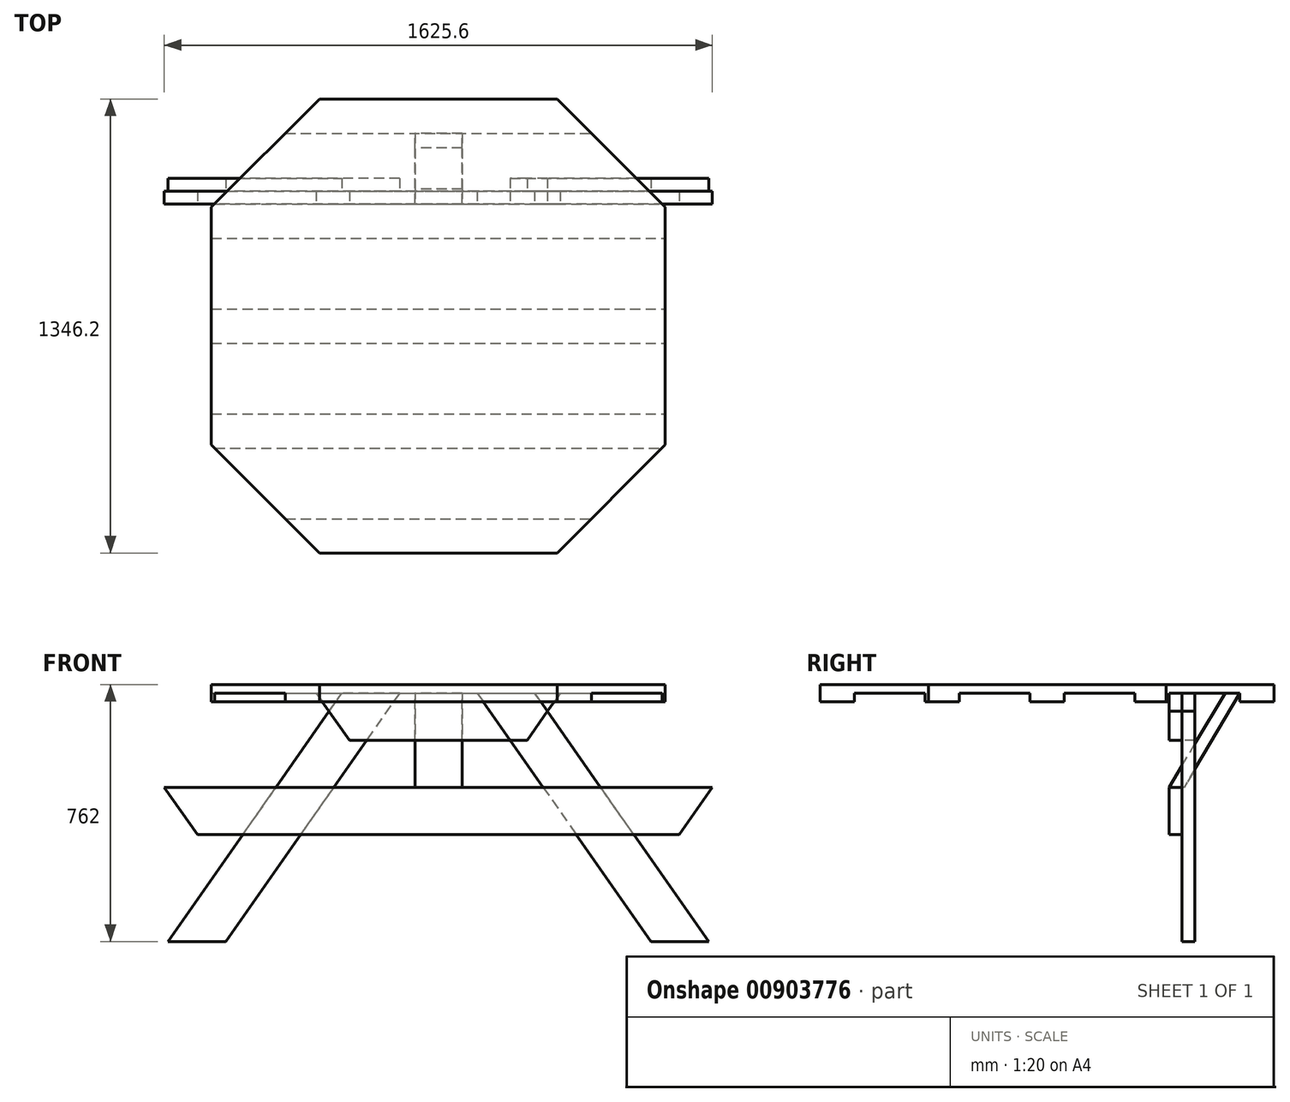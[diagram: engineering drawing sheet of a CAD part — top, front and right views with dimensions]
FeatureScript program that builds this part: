
annotation { "Feature Type Name" : "Feature", "Feature Type Description" : "" }
export const myFeature = defineFeature(function(context is Context, id is Id, definition is map)
    precondition{}
    {
        {
            var Q0;
            Q0=qCreatedBy(makeId("Top.planeOp"),FACE);
            var sketch = newSketch(context, id + "F0", { "sketchPlane" : qUnion([Q0])});
            skPoint(sketch, "E0.middle", {"position": v(0, 0) * mm});
            skLineSegment(sketch, "E1", {"start": v(-362.6, 663.57) * mm, "end": v(-362.6, -663.58) * mm});
            skLineSegment(sketch, "E2", {"start": v(361.3, 663.58) * mm, "end": v(361.3, -663.58) * mm});
            skLineSegment(sketch, "E3", {"start": v(-0.66, 673.1) * mm, "end": v(-0.66, -673.1) * mm});
            skPoint(sketch, "E4", {"position": v(-673.76, 0) * mm});
            skPoint(sketch, "E5", {"position": v(672.44, 0) * mm});
            skLineSegment(sketch, "E6", {"start": v(-673.76, 352.43) * mm, "end": v(-673.76, -352.43) * mm});
            skLineSegment(sketch, "E7", {"start": v(672.44, 352.43) * mm, "end": v(672.44, -352.43) * mm});
            skLineSegment(sketch, "E8", {"start": v(-353.08, -673.1) * mm, "end": v(351.77, -673.1) * mm});
            skLineSegment(sketch, "E9", {"start": v(-353.08, 673.1) * mm, "end": v(351.77, 673.1) * mm});
            skPoint(sketch, "E10", {"position": v(-0.66, -673.1) * mm});
            skPoint(sketch, "E11", {"position": v(-0.66, 673.1) * mm});
            skLineSegment(sketch, "E12", {"start": v(-673.76, 352.43) * mm, "end": v(-353.08, 673.1) * mm});
            skLineSegment(sketch, "E13", {"start": v(351.77, 673.1) * mm, "end": v(672.44, 352.42) * mm});
            skLineSegment(sketch, "E14", {"start": v(351.77, -673.1) * mm, "end": v(672.44, -352.43) * mm});
            skLineSegment(sketch, "E15", {"start": v(-353.08, -673.1) * mm, "end": v(-673.76, -352.43) * mm});
            skLineSegment(sketch, "E16", {"start": v(-454.68, -571.5) * mm, "end": v(453.37, -571.5) * mm});
            skLineSegment(sketch, "E17", {"start": v(-673.76, 50.8) * mm, "end": v(672.44, 50.8) * mm});
            skLineSegment(sketch, "E18", {"start": v(-673.76, -50.8) * mm, "end": v(672.44, -50.8) * mm});
            skLineSegment(sketch, "E19", {"start": v(-673.76, 260.35) * mm, "end": v(672.44, 260.35) * mm});
            skLineSegment(sketch, "E20", {"start": v(-673.76, -260.35) * mm, "end": v(672.44, -260.35) * mm});
            skLineSegment(sketch, "E21", {"start": v(-454.68, 571.5) * mm, "end": v(453.37, 571.5) * mm});
            skLineSegment(sketch, "E22", {"start": v(-664.23, -361.95) * mm, "end": v(662.92, -361.95) * mm});
            skLineSegment(sketch, "E23", {"start": v(-664.23, 361.95) * mm, "end": v(662.92, 361.95) * mm});
            skSolve(sketch);
        }
        {
            var Q0;
            {var subQ0=sQuery(id+"F0.wireOp",EDGE,"E12");var subQ1=sQuery(id+"F0.wireOp",EDGE,"E1");var subQ2=makeQuery(id+"F0.imprint","INTERSECT",VERTEX,{"derivedFrom":[subQ1,subQ0]});Q0=makeQuery(id+"F0.imprint","IMPRINT",FACE,{"disambiguationData":[TD([[makeQuery(id+"F0.imprint","IMPRINT",EDGE,{"disambiguationData":[TD([[subQ2,-1.0]])],"derivedFrom":subQ1}),-1.0]])]});}
            var Q1;
            {var subQ3=sQuery(id+"F0.wireOp",EDGE,"E1");var subQ7=sQuery(id+"F0.wireOp",EDGE,"E23");var subQ9=makeQuery(id+"F0.imprint","INTERSECT",VERTEX,{"derivedFrom":[subQ3,subQ7]});Q1=makeQuery(id+"F0.imprint","IMPRINT",FACE,{"disambiguationData":[TD([[makeQuery(id+"F0.imprint","IMPRINT",EDGE,{"disambiguationData":[TD([[subQ9,-1.0]])],"derivedFrom":subQ3}),-1.0]])]});}
            var Q2;
            {var subQ0=sQuery(id+"F0.wireOp",EDGE,"E17");var subQ1=sQuery(id+"F0.wireOp",EDGE,"E1");var subQ2=makeQuery(id+"F0.imprint","INTERSECT",VERTEX,{"derivedFrom":[subQ1,subQ0]});Q2=makeQuery(id+"F0.imprint","IMPRINT",FACE,{"disambiguationData":[TD([[makeQuery(id+"F0.imprint","IMPRINT",EDGE,{"disambiguationData":[TD([[subQ2,-1.0]])],"derivedFrom":subQ1}),-1.0]])]});}
            var Q3;
            {var subQ0=sQuery(id+"F0.wireOp",EDGE,"E20");var subQ3=sQuery(id+"F0.wireOp",EDGE,"E1");var subQ4=makeQuery(id+"F0.imprint","INTERSECT",VERTEX,{"derivedFrom":[subQ3,subQ0]});Q3=makeQuery(id+"F0.imprint","IMPRINT",FACE,{"disambiguationData":[TD([[makeQuery(id+"F0.imprint","IMPRINT",EDGE,{"disambiguationData":[TD([[subQ4,-1.0]])],"derivedFrom":subQ3}),-1.0]])]});}
            var Q4;
            {var subQ0=sQuery(id+"F0.wireOp",EDGE,"E15");var subQ1=sQuery(id+"F0.wireOp",EDGE,"E1");var subQ2=makeQuery(id+"F0.imprint","INTERSECT",VERTEX,{"derivedFrom":[subQ1,subQ0]});Q4=makeQuery(id+"F0.imprint","IMPRINT",FACE,{"disambiguationData":[TD([[makeQuery(id+"F0.imprint","IMPRINT",EDGE,{"disambiguationData":[TD([[subQ2,1.0]])],"derivedFrom":subQ1}),-1.0]])]});}
            extrude(context, id + "F1", {"entities" : qUnion([Q0, Q1, Q2, Q3, Q4]), "oppositeDirection" : true, "depth" : 25.4 * mm, "offsetDistance" : 25.4 * mm});
        }
        {
            var Q0;
            {var subQ0=sQuery(id+"F0.wireOp",EDGE,"E12");var subQ1=sQuery(id+"F0.wireOp",EDGE,"E1");var subQ2=makeQuery(id+"F0.imprint","INTERSECT",VERTEX,{"derivedFrom":[subQ1,subQ0]});Q0=makeQuery(id+"F0.imprint","IMPRINT",FACE,{"disambiguationData":[TD([[makeQuery(id+"F0.imprint","IMPRINT",EDGE,{"disambiguationData":[TD([[subQ2,-1.0]])],"derivedFrom":subQ1}),-1.0]])]});}
            var Q1;
            {var subQ0=sQuery(id+"F0.wireOp",EDGE,"E21");var subQ1=sQuery(id+"F0.wireOp",EDGE,"E1");var subQ2=makeQuery(id+"F0.imprint","INTERSECT",VERTEX,{"derivedFrom":[subQ1,subQ0]});Q1=makeQuery(id+"F0.imprint","IMPRINT",FACE,{"disambiguationData":[TD([[makeQuery(id+"F0.imprint","IMPRINT",EDGE,{"disambiguationData":[TD([[subQ2,-1.0]])],"derivedFrom":subQ1}),-1.0]])]});}
            var Q2;
            {var subQ3=sQuery(id+"F0.wireOp",EDGE,"E1");var subQ7=sQuery(id+"F0.wireOp",EDGE,"E23");var subQ9=makeQuery(id+"F0.imprint","INTERSECT",VERTEX,{"derivedFrom":[subQ3,subQ7]});Q2=makeQuery(id+"F0.imprint","IMPRINT",FACE,{"disambiguationData":[TD([[makeQuery(id+"F0.imprint","IMPRINT",EDGE,{"disambiguationData":[TD([[subQ9,-1.0]])],"derivedFrom":subQ3}),-1.0]])]});}
            var Q3;
            {var subQ0=sQuery(id+"F0.wireOp",EDGE,"E19");var subQ1=sQuery(id+"F0.wireOp",EDGE,"E1");var subQ2=makeQuery(id+"F0.imprint","INTERSECT",VERTEX,{"derivedFrom":[subQ1,subQ0]});Q3=makeQuery(id+"F0.imprint","IMPRINT",FACE,{"disambiguationData":[TD([[makeQuery(id+"F0.imprint","IMPRINT",EDGE,{"disambiguationData":[TD([[subQ2,-1.0]])],"derivedFrom":subQ1}),-1.0]])]});}
            var Q4;
            {var subQ0=sQuery(id+"F0.wireOp",EDGE,"E17");var subQ1=sQuery(id+"F0.wireOp",EDGE,"E1");var subQ2=makeQuery(id+"F0.imprint","INTERSECT",VERTEX,{"derivedFrom":[subQ1,subQ0]});Q4=makeQuery(id+"F0.imprint","IMPRINT",FACE,{"disambiguationData":[TD([[makeQuery(id+"F0.imprint","IMPRINT",EDGE,{"disambiguationData":[TD([[subQ2,-1.0]])],"derivedFrom":subQ1}),-1.0]])]});}
            var Q5;
            {var subQ0=sQuery(id+"F0.wireOp",EDGE,"E18");var subQ1=sQuery(id+"F0.wireOp",EDGE,"E1");var subQ2=makeQuery(id+"F0.imprint","INTERSECT",VERTEX,{"derivedFrom":[subQ1,subQ0]});Q5=makeQuery(id+"F0.imprint","IMPRINT",FACE,{"disambiguationData":[TD([[makeQuery(id+"F0.imprint","IMPRINT",EDGE,{"disambiguationData":[TD([[subQ2,-1.0]])],"derivedFrom":subQ1}),-1.0]])]});}
            var Q6;
            {var subQ0=sQuery(id+"F0.wireOp",EDGE,"E20");var subQ3=sQuery(id+"F0.wireOp",EDGE,"E1");var subQ4=makeQuery(id+"F0.imprint","INTERSECT",VERTEX,{"derivedFrom":[subQ3,subQ0]});Q6=makeQuery(id+"F0.imprint","IMPRINT",FACE,{"disambiguationData":[TD([[makeQuery(id+"F0.imprint","IMPRINT",EDGE,{"disambiguationData":[TD([[subQ4,-1.0]])],"derivedFrom":subQ3}),-1.0]])]});}
            var Q7;
            {var subQ0=sQuery(id+"F0.wireOp",EDGE,"E22");var subQ1=sQuery(id+"F0.wireOp",EDGE,"E1");var subQ2=makeQuery(id+"F0.imprint","INTERSECT",VERTEX,{"derivedFrom":[subQ1,subQ0]});Q7=makeQuery(id+"F0.imprint","IMPRINT",FACE,{"disambiguationData":[TD([[makeQuery(id+"F0.imprint","IMPRINT",EDGE,{"disambiguationData":[TD([[subQ2,-1.0]])],"derivedFrom":subQ1}),-1.0]])]});}
            var Q8;
            {var subQ0=sQuery(id+"F0.wireOp",EDGE,"E15");var subQ1=sQuery(id+"F0.wireOp",EDGE,"E1");var subQ2=makeQuery(id+"F0.imprint","INTERSECT",VERTEX,{"derivedFrom":[subQ1,subQ0]});Q8=makeQuery(id+"F0.imprint","IMPRINT",FACE,{"disambiguationData":[TD([[makeQuery(id+"F0.imprint","IMPRINT",EDGE,{"disambiguationData":[TD([[subQ2,1.0]])],"derivedFrom":subQ1}),-1.0]])]});}
            extrude(context, id + "F2", {"entities" : qUnion([Q0, Q1, Q2, Q3, Q4, Q5, Q6, Q7, Q8]), "operationType" : NewBodyOperationType.ADD, "depth" : 25.4 * mm, "offsetDistance" : 25.4 * mm});
        }
        {
            var Q0;
            {var subQ0=sQuery(id+"F0.wireOp",EDGE,"E13");var subQ1=sQuery(id+"F0.wireOp",EDGE,"E2");var subQ2=makeQuery(id+"F0.imprint","INTERSECT",VERTEX,{"derivedFrom":[subQ1,subQ0]});Q0=makeQuery(id+"F0.imprint","IMPRINT",FACE,{"disambiguationData":[TD([[makeQuery(id+"F0.imprint","IMPRINT",EDGE,{"disambiguationData":[TD([[subQ2,-1.0]])],"derivedFrom":subQ1}),1.0]])]});}
            var Q1;
            {var subQ3=sQuery(id+"F0.wireOp",EDGE,"E23");var subQ7=sQuery(id+"F0.wireOp",EDGE,"E2");var subQ9=makeQuery(id+"F0.imprint","INTERSECT",VERTEX,{"derivedFrom":[subQ7,subQ3]});Q1=makeQuery(id+"F0.imprint","IMPRINT",FACE,{"disambiguationData":[TD([[makeQuery(id+"F0.imprint","IMPRINT",EDGE,{"disambiguationData":[TD([[subQ9,-1.0]])],"derivedFrom":subQ7}),1.0]])]});}
            var Q2;
            {var subQ0=sQuery(id+"F0.wireOp",EDGE,"E17");var subQ1=sQuery(id+"F0.wireOp",EDGE,"E2");var subQ2=makeQuery(id+"F0.imprint","INTERSECT",VERTEX,{"derivedFrom":[subQ1,subQ0]});Q2=makeQuery(id+"F0.imprint","IMPRINT",FACE,{"disambiguationData":[TD([[makeQuery(id+"F0.imprint","IMPRINT",EDGE,{"disambiguationData":[TD([[subQ2,-1.0]])],"derivedFrom":subQ1}),1.0]])]});}
            var Q3;
            {var subQ5=sQuery(id+"F0.wireOp",EDGE,"E20");var subQ7=sQuery(id+"F0.wireOp",EDGE,"E2");var subQ8=makeQuery(id+"F0.imprint","INTERSECT",VERTEX,{"derivedFrom":[subQ7,subQ5]});Q3=makeQuery(id+"F0.imprint","IMPRINT",FACE,{"disambiguationData":[TD([[makeQuery(id+"F0.imprint","IMPRINT",EDGE,{"disambiguationData":[TD([[subQ8,-1.0]])],"derivedFrom":subQ7}),1.0]])]});}
            var Q4;
            {var subQ0=sQuery(id+"F0.wireOp",EDGE,"E14");var subQ1=sQuery(id+"F0.wireOp",EDGE,"E2");var subQ2=makeQuery(id+"F0.imprint","INTERSECT",VERTEX,{"derivedFrom":[subQ1,subQ0]});Q4=makeQuery(id+"F0.imprint","IMPRINT",FACE,{"disambiguationData":[TD([[makeQuery(id+"F0.imprint","IMPRINT",EDGE,{"disambiguationData":[TD([[subQ2,1.0]])],"derivedFrom":subQ1}),1.0]])]});}
            extrude(context, id + "F3", {"entities" : qUnion([Q0, Q1, Q2, Q3, Q4]), "oppositeDirection" : true, "depth" : 25.4 * mm, "offsetDistance" : 25.4 * mm});
        }
        {
            var Q0;
            {var subQ0=sQuery(id+"F0.wireOp",EDGE,"E13");var subQ1=sQuery(id+"F0.wireOp",EDGE,"E2");var subQ2=makeQuery(id+"F0.imprint","INTERSECT",VERTEX,{"derivedFrom":[subQ1,subQ0]});Q0=makeQuery(id+"F0.imprint","IMPRINT",FACE,{"disambiguationData":[TD([[makeQuery(id+"F0.imprint","IMPRINT",EDGE,{"disambiguationData":[TD([[subQ2,-1.0]])],"derivedFrom":subQ1}),1.0]])]});}
            var Q1;
            {var subQ0=sQuery(id+"F0.wireOp",EDGE,"E21");var subQ1=sQuery(id+"F0.wireOp",EDGE,"E2");var subQ2=makeQuery(id+"F0.imprint","INTERSECT",VERTEX,{"derivedFrom":[subQ1,subQ0]});Q1=makeQuery(id+"F0.imprint","IMPRINT",FACE,{"disambiguationData":[TD([[makeQuery(id+"F0.imprint","IMPRINT",EDGE,{"disambiguationData":[TD([[subQ2,-1.0]])],"derivedFrom":subQ1}),1.0]])]});}
            var Q2;
            {var subQ3=sQuery(id+"F0.wireOp",EDGE,"E23");var subQ7=sQuery(id+"F0.wireOp",EDGE,"E2");var subQ9=makeQuery(id+"F0.imprint","INTERSECT",VERTEX,{"derivedFrom":[subQ7,subQ3]});Q2=makeQuery(id+"F0.imprint","IMPRINT",FACE,{"disambiguationData":[TD([[makeQuery(id+"F0.imprint","IMPRINT",EDGE,{"disambiguationData":[TD([[subQ9,-1.0]])],"derivedFrom":subQ7}),1.0]])]});}
            var Q3;
            {var subQ0=sQuery(id+"F0.wireOp",EDGE,"E19");var subQ1=sQuery(id+"F0.wireOp",EDGE,"E2");var subQ2=makeQuery(id+"F0.imprint","INTERSECT",VERTEX,{"derivedFrom":[subQ1,subQ0]});Q3=makeQuery(id+"F0.imprint","IMPRINT",FACE,{"disambiguationData":[TD([[makeQuery(id+"F0.imprint","IMPRINT",EDGE,{"disambiguationData":[TD([[subQ2,-1.0]])],"derivedFrom":subQ1}),1.0]])]});}
            var Q4;
            {var subQ0=sQuery(id+"F0.wireOp",EDGE,"E17");var subQ1=sQuery(id+"F0.wireOp",EDGE,"E2");var subQ2=makeQuery(id+"F0.imprint","INTERSECT",VERTEX,{"derivedFrom":[subQ1,subQ0]});Q4=makeQuery(id+"F0.imprint","IMPRINT",FACE,{"disambiguationData":[TD([[makeQuery(id+"F0.imprint","IMPRINT",EDGE,{"disambiguationData":[TD([[subQ2,-1.0]])],"derivedFrom":subQ1}),1.0]])]});}
            var Q5;
            {var subQ0=sQuery(id+"F0.wireOp",EDGE,"E18");var subQ1=sQuery(id+"F0.wireOp",EDGE,"E2");var subQ2=makeQuery(id+"F0.imprint","INTERSECT",VERTEX,{"derivedFrom":[subQ1,subQ0]});Q5=makeQuery(id+"F0.imprint","IMPRINT",FACE,{"disambiguationData":[TD([[makeQuery(id+"F0.imprint","IMPRINT",EDGE,{"disambiguationData":[TD([[subQ2,-1.0]])],"derivedFrom":subQ1}),1.0]])]});}
            var Q6;
            {var subQ5=sQuery(id+"F0.wireOp",EDGE,"E20");var subQ7=sQuery(id+"F0.wireOp",EDGE,"E2");var subQ8=makeQuery(id+"F0.imprint","INTERSECT",VERTEX,{"derivedFrom":[subQ7,subQ5]});Q6=makeQuery(id+"F0.imprint","IMPRINT",FACE,{"disambiguationData":[TD([[makeQuery(id+"F0.imprint","IMPRINT",EDGE,{"disambiguationData":[TD([[subQ8,-1.0]])],"derivedFrom":subQ7}),1.0]])]});}
            var Q7;
            {var subQ0=sQuery(id+"F0.wireOp",EDGE,"E22");var subQ1=sQuery(id+"F0.wireOp",EDGE,"E2");var subQ2=makeQuery(id+"F0.imprint","INTERSECT",VERTEX,{"derivedFrom":[subQ1,subQ0]});Q7=makeQuery(id+"F0.imprint","IMPRINT",FACE,{"disambiguationData":[TD([[makeQuery(id+"F0.imprint","IMPRINT",EDGE,{"disambiguationData":[TD([[subQ2,-1.0]])],"derivedFrom":subQ1}),1.0]])]});}
            var Q8;
            {var subQ0=sQuery(id+"F0.wireOp",EDGE,"E14");var subQ1=sQuery(id+"F0.wireOp",EDGE,"E2");var subQ2=makeQuery(id+"F0.imprint","INTERSECT",VERTEX,{"derivedFrom":[subQ1,subQ0]});Q8=makeQuery(id+"F0.imprint","IMPRINT",FACE,{"disambiguationData":[TD([[makeQuery(id+"F0.imprint","IMPRINT",EDGE,{"disambiguationData":[TD([[subQ2,1.0]])],"derivedFrom":subQ1}),1.0]])]});}
            extrude(context, id + "F4", {"entities" : qUnion([Q0, Q1, Q2, Q3, Q4, Q5, Q6, Q7, Q8]), "operationType" : NewBodyOperationType.ADD, "depth" : 25.4 * mm, "offsetDistance" : 25.4 * mm});
        }
        {
            var Q0;
            {var subQ0=sQuery(id+"F0.wireOp",EDGE,"E12");var subQ1=sQuery(id+"F0.wireOp",EDGE,"E1");var subQ2=makeQuery(id+"F0.imprint","INTERSECT",VERTEX,{"derivedFrom":[subQ1,subQ0]});Q0=makeQuery(id+"F0.imprint","IMPRINT",FACE,{"disambiguationData":[TD([[makeQuery(id+"F0.imprint","IMPRINT",EDGE,{"disambiguationData":[TD([[subQ2,-1.0]])],"derivedFrom":subQ1}),1.0]])]});}
            var Q1;
            {var subQ0=sQuery(id+"F0.wireOp",EDGE,"E13");var subQ1=sQuery(id+"F0.wireOp",EDGE,"E2");var subQ2=makeQuery(id+"F0.imprint","INTERSECT",VERTEX,{"derivedFrom":[subQ1,subQ0]});Q1=makeQuery(id+"F0.imprint","IMPRINT",FACE,{"disambiguationData":[TD([[makeQuery(id+"F0.imprint","IMPRINT",EDGE,{"disambiguationData":[TD([[subQ2,-1.0]])],"derivedFrom":subQ1}),-1.0]])]});}
            var Q2;
            {var subQ0=sQuery(id+"F0.wireOp",EDGE,"E23");var subQ1=sQuery(id+"F0.wireOp",EDGE,"E1");var subQ2=makeQuery(id+"F0.imprint","INTERSECT",VERTEX,{"derivedFrom":[subQ1,subQ0]});Q2=makeQuery(id+"F0.imprint","IMPRINT",FACE,{"disambiguationData":[TD([[makeQuery(id+"F0.imprint","IMPRINT",EDGE,{"disambiguationData":[TD([[subQ2,-1.0]])],"derivedFrom":subQ1}),1.0]])]});}
            var Q3;
            {var subQ0=sQuery(id+"F0.wireOp",EDGE,"E23");var subQ1=sQuery(id+"F0.wireOp",EDGE,"E2");var subQ2=makeQuery(id+"F0.imprint","INTERSECT",VERTEX,{"derivedFrom":[subQ1,subQ0]});Q3=makeQuery(id+"F0.imprint","IMPRINT",FACE,{"disambiguationData":[TD([[makeQuery(id+"F0.imprint","IMPRINT",EDGE,{"disambiguationData":[TD([[subQ2,-1.0]])],"derivedFrom":subQ1}),-1.0]])]});}
            var Q4;
            {var subQ0=sQuery(id+"F0.wireOp",EDGE,"E17");var subQ1=sQuery(id+"F0.wireOp",EDGE,"E1");var subQ2=makeQuery(id+"F0.imprint","INTERSECT",VERTEX,{"derivedFrom":[subQ1,subQ0]});Q4=makeQuery(id+"F0.imprint","IMPRINT",FACE,{"disambiguationData":[TD([[makeQuery(id+"F0.imprint","IMPRINT",EDGE,{"disambiguationData":[TD([[subQ2,-1.0]])],"derivedFrom":subQ1}),1.0]])]});}
            var Q5;
            {var subQ0=sQuery(id+"F0.wireOp",EDGE,"E17");var subQ1=sQuery(id+"F0.wireOp",EDGE,"E2");var subQ2=makeQuery(id+"F0.imprint","INTERSECT",VERTEX,{"derivedFrom":[subQ1,subQ0]});Q5=makeQuery(id+"F0.imprint","IMPRINT",FACE,{"disambiguationData":[TD([[makeQuery(id+"F0.imprint","IMPRINT",EDGE,{"disambiguationData":[TD([[subQ2,-1.0]])],"derivedFrom":subQ1}),-1.0]])]});}
            var Q6;
            {var subQ0=sQuery(id+"F0.wireOp",EDGE,"E20");var subQ1=sQuery(id+"F0.wireOp",EDGE,"E1");var subQ2=makeQuery(id+"F0.imprint","INTERSECT",VERTEX,{"derivedFrom":[subQ1,subQ0]});Q6=makeQuery(id+"F0.imprint","IMPRINT",FACE,{"disambiguationData":[TD([[makeQuery(id+"F0.imprint","IMPRINT",EDGE,{"disambiguationData":[TD([[subQ2,-1.0]])],"derivedFrom":subQ1}),1.0]])]});}
            var Q7;
            {var subQ0=sQuery(id+"F0.wireOp",EDGE,"E20");var subQ1=sQuery(id+"F0.wireOp",EDGE,"E2");var subQ2=makeQuery(id+"F0.imprint","INTERSECT",VERTEX,{"derivedFrom":[subQ1,subQ0]});Q7=makeQuery(id+"F0.imprint","IMPRINT",FACE,{"disambiguationData":[TD([[makeQuery(id+"F0.imprint","IMPRINT",EDGE,{"disambiguationData":[TD([[subQ2,-1.0]])],"derivedFrom":subQ1}),-1.0]])]});}
            var Q8;
            {var subQ3=sQuery(id+"F0.wireOp",EDGE,"E15");var subQ7=sQuery(id+"F0.wireOp",EDGE,"E1");var subQ8=makeQuery(id+"F0.imprint","INTERSECT",VERTEX,{"derivedFrom":[subQ7,subQ3]});Q8=makeQuery(id+"F0.imprint","IMPRINT",FACE,{"disambiguationData":[TD([[makeQuery(id+"F0.imprint","IMPRINT",EDGE,{"disambiguationData":[TD([[subQ8,1.0]])],"derivedFrom":subQ7}),1.0]])]});}
            var Q9;
            {var subQ0=sQuery(id+"F0.wireOp",EDGE,"E14");var subQ1=sQuery(id+"F0.wireOp",EDGE,"E2");var subQ2=makeQuery(id+"F0.imprint","INTERSECT",VERTEX,{"derivedFrom":[subQ1,subQ0]});Q9=makeQuery(id+"F0.imprint","IMPRINT",FACE,{"disambiguationData":[TD([[makeQuery(id+"F0.imprint","IMPRINT",EDGE,{"disambiguationData":[TD([[subQ2,1.0]])],"derivedFrom":subQ1}),-1.0]])]});}
            extrude(context, id + "F5", {"entities" : qUnion([Q0, Q1, Q2, Q3, Q4, Q5, Q6, Q7, Q8, Q9]), "oppositeDirection" : true, "depth" : 25.4 * mm, "offsetDistance" : 25.4 * mm});
        }
        {
            var Q0;
            {var subQ0=sQuery(id+"F0.wireOp",EDGE,"E21");var subQ1=sQuery(id+"F0.wireOp",EDGE,"E1");var subQ2=makeQuery(id+"F0.imprint","INTERSECT",VERTEX,{"derivedFrom":[subQ1,subQ0]});Q0=makeQuery(id+"F0.imprint","IMPRINT",FACE,{"disambiguationData":[TD([[makeQuery(id+"F0.imprint","IMPRINT",EDGE,{"disambiguationData":[TD([[subQ2,-1.0]])],"derivedFrom":subQ1}),1.0]])]});}
            var Q1;
            {var subQ0=sQuery(id+"F0.wireOp",EDGE,"E21");var subQ1=sQuery(id+"F0.wireOp",EDGE,"E2");var subQ2=makeQuery(id+"F0.imprint","INTERSECT",VERTEX,{"derivedFrom":[subQ1,subQ0]});Q1=makeQuery(id+"F0.imprint","IMPRINT",FACE,{"disambiguationData":[TD([[makeQuery(id+"F0.imprint","IMPRINT",EDGE,{"disambiguationData":[TD([[subQ2,-1.0]])],"derivedFrom":subQ1}),-1.0]])]});}
            var Q2;
            {var subQ0=sQuery(id+"F0.wireOp",EDGE,"E12");var subQ1=sQuery(id+"F0.wireOp",EDGE,"E1");var subQ2=makeQuery(id+"F0.imprint","INTERSECT",VERTEX,{"derivedFrom":[subQ1,subQ0]});Q2=makeQuery(id+"F0.imprint","IMPRINT",FACE,{"disambiguationData":[TD([[makeQuery(id+"F0.imprint","IMPRINT",EDGE,{"disambiguationData":[TD([[subQ2,-1.0]])],"derivedFrom":subQ1}),1.0]])]});}
            var Q3;
            {var subQ0=sQuery(id+"F0.wireOp",EDGE,"E13");var subQ1=sQuery(id+"F0.wireOp",EDGE,"E2");var subQ2=makeQuery(id+"F0.imprint","INTERSECT",VERTEX,{"derivedFrom":[subQ1,subQ0]});Q3=makeQuery(id+"F0.imprint","IMPRINT",FACE,{"disambiguationData":[TD([[makeQuery(id+"F0.imprint","IMPRINT",EDGE,{"disambiguationData":[TD([[subQ2,-1.0]])],"derivedFrom":subQ1}),-1.0]])]});}
            var Q4;
            {var subQ0=sQuery(id+"F0.wireOp",EDGE,"E23");var subQ1=sQuery(id+"F0.wireOp",EDGE,"E1");var subQ2=makeQuery(id+"F0.imprint","INTERSECT",VERTEX,{"derivedFrom":[subQ1,subQ0]});Q4=makeQuery(id+"F0.imprint","IMPRINT",FACE,{"disambiguationData":[TD([[makeQuery(id+"F0.imprint","IMPRINT",EDGE,{"disambiguationData":[TD([[subQ2,-1.0]])],"derivedFrom":subQ1}),1.0]])]});}
            var Q5;
            {var subQ0=sQuery(id+"F0.wireOp",EDGE,"E23");var subQ1=sQuery(id+"F0.wireOp",EDGE,"E2");var subQ2=makeQuery(id+"F0.imprint","INTERSECT",VERTEX,{"derivedFrom":[subQ1,subQ0]});Q5=makeQuery(id+"F0.imprint","IMPRINT",FACE,{"disambiguationData":[TD([[makeQuery(id+"F0.imprint","IMPRINT",EDGE,{"disambiguationData":[TD([[subQ2,-1.0]])],"derivedFrom":subQ1}),-1.0]])]});}
            var Q6;
            {var subQ0=sQuery(id+"F0.wireOp",EDGE,"E19");var subQ1=sQuery(id+"F0.wireOp",EDGE,"E1");var subQ2=makeQuery(id+"F0.imprint","INTERSECT",VERTEX,{"derivedFrom":[subQ1,subQ0]});Q6=makeQuery(id+"F0.imprint","IMPRINT",FACE,{"disambiguationData":[TD([[makeQuery(id+"F0.imprint","IMPRINT",EDGE,{"disambiguationData":[TD([[subQ2,-1.0]])],"derivedFrom":subQ1}),1.0]])]});}
            var Q7;
            {var subQ0=sQuery(id+"F0.wireOp",EDGE,"E19");var subQ1=sQuery(id+"F0.wireOp",EDGE,"E2");var subQ2=makeQuery(id+"F0.imprint","INTERSECT",VERTEX,{"derivedFrom":[subQ1,subQ0]});Q7=makeQuery(id+"F0.imprint","IMPRINT",FACE,{"disambiguationData":[TD([[makeQuery(id+"F0.imprint","IMPRINT",EDGE,{"disambiguationData":[TD([[subQ2,-1.0]])],"derivedFrom":subQ1}),-1.0]])]});}
            var Q8;
            {var subQ0=sQuery(id+"F0.wireOp",EDGE,"E17");var subQ1=sQuery(id+"F0.wireOp",EDGE,"E2");var subQ2=makeQuery(id+"F0.imprint","INTERSECT",VERTEX,{"derivedFrom":[subQ1,subQ0]});Q8=makeQuery(id+"F0.imprint","IMPRINT",FACE,{"disambiguationData":[TD([[makeQuery(id+"F0.imprint","IMPRINT",EDGE,{"disambiguationData":[TD([[subQ2,-1.0]])],"derivedFrom":subQ1}),-1.0]])]});}
            var Q9;
            {var subQ0=sQuery(id+"F0.wireOp",EDGE,"E17");var subQ1=sQuery(id+"F0.wireOp",EDGE,"E1");var subQ2=makeQuery(id+"F0.imprint","INTERSECT",VERTEX,{"derivedFrom":[subQ1,subQ0]});Q9=makeQuery(id+"F0.imprint","IMPRINT",FACE,{"disambiguationData":[TD([[makeQuery(id+"F0.imprint","IMPRINT",EDGE,{"disambiguationData":[TD([[subQ2,-1.0]])],"derivedFrom":subQ1}),1.0]])]});}
            var Q10;
            {var subQ0=sQuery(id+"F0.wireOp",EDGE,"E18");var subQ1=sQuery(id+"F0.wireOp",EDGE,"E1");var subQ2=makeQuery(id+"F0.imprint","INTERSECT",VERTEX,{"derivedFrom":[subQ1,subQ0]});Q10=makeQuery(id+"F0.imprint","IMPRINT",FACE,{"disambiguationData":[TD([[makeQuery(id+"F0.imprint","IMPRINT",EDGE,{"disambiguationData":[TD([[subQ2,-1.0]])],"derivedFrom":subQ1}),1.0]])]});}
            var Q11;
            {var subQ0=sQuery(id+"F0.wireOp",EDGE,"E18");var subQ1=sQuery(id+"F0.wireOp",EDGE,"E2");var subQ2=makeQuery(id+"F0.imprint","INTERSECT",VERTEX,{"derivedFrom":[subQ1,subQ0]});Q11=makeQuery(id+"F0.imprint","IMPRINT",FACE,{"disambiguationData":[TD([[makeQuery(id+"F0.imprint","IMPRINT",EDGE,{"disambiguationData":[TD([[subQ2,-1.0]])],"derivedFrom":subQ1}),-1.0]])]});}
            var Q12;
            {var subQ0=sQuery(id+"F0.wireOp",EDGE,"E20");var subQ1=sQuery(id+"F0.wireOp",EDGE,"E2");var subQ2=makeQuery(id+"F0.imprint","INTERSECT",VERTEX,{"derivedFrom":[subQ1,subQ0]});Q12=makeQuery(id+"F0.imprint","IMPRINT",FACE,{"disambiguationData":[TD([[makeQuery(id+"F0.imprint","IMPRINT",EDGE,{"disambiguationData":[TD([[subQ2,-1.0]])],"derivedFrom":subQ1}),-1.0]])]});}
            var Q13;
            {var subQ0=sQuery(id+"F0.wireOp",EDGE,"E20");var subQ1=sQuery(id+"F0.wireOp",EDGE,"E1");var subQ2=makeQuery(id+"F0.imprint","INTERSECT",VERTEX,{"derivedFrom":[subQ1,subQ0]});Q13=makeQuery(id+"F0.imprint","IMPRINT",FACE,{"disambiguationData":[TD([[makeQuery(id+"F0.imprint","IMPRINT",EDGE,{"disambiguationData":[TD([[subQ2,-1.0]])],"derivedFrom":subQ1}),1.0]])]});}
            var Q14;
            {var subQ0=sQuery(id+"F0.wireOp",EDGE,"E22");var subQ1=sQuery(id+"F0.wireOp",EDGE,"E1");var subQ2=makeQuery(id+"F0.imprint","INTERSECT",VERTEX,{"derivedFrom":[subQ1,subQ0]});Q14=makeQuery(id+"F0.imprint","IMPRINT",FACE,{"disambiguationData":[TD([[makeQuery(id+"F0.imprint","IMPRINT",EDGE,{"disambiguationData":[TD([[subQ2,-1.0]])],"derivedFrom":subQ1}),1.0]])]});}
            var Q15;
            {var subQ0=sQuery(id+"F0.wireOp",EDGE,"E22");var subQ1=sQuery(id+"F0.wireOp",EDGE,"E2");var subQ2=makeQuery(id+"F0.imprint","INTERSECT",VERTEX,{"derivedFrom":[subQ1,subQ0]});Q15=makeQuery(id+"F0.imprint","IMPRINT",FACE,{"disambiguationData":[TD([[makeQuery(id+"F0.imprint","IMPRINT",EDGE,{"disambiguationData":[TD([[subQ2,-1.0]])],"derivedFrom":subQ1}),-1.0]])]});}
            var Q16;
            {var subQ0=sQuery(id+"F0.wireOp",EDGE,"E14");var subQ1=sQuery(id+"F0.wireOp",EDGE,"E2");var subQ2=makeQuery(id+"F0.imprint","INTERSECT",VERTEX,{"derivedFrom":[subQ1,subQ0]});Q16=makeQuery(id+"F0.imprint","IMPRINT",FACE,{"disambiguationData":[TD([[makeQuery(id+"F0.imprint","IMPRINT",EDGE,{"disambiguationData":[TD([[subQ2,1.0]])],"derivedFrom":subQ1}),-1.0]])]});}
            var Q17;
            {var subQ3=sQuery(id+"F0.wireOp",EDGE,"E15");var subQ7=sQuery(id+"F0.wireOp",EDGE,"E1");var subQ8=makeQuery(id+"F0.imprint","INTERSECT",VERTEX,{"derivedFrom":[subQ7,subQ3]});Q17=makeQuery(id+"F0.imprint","IMPRINT",FACE,{"disambiguationData":[TD([[makeQuery(id+"F0.imprint","IMPRINT",EDGE,{"disambiguationData":[TD([[subQ8,1.0]])],"derivedFrom":subQ7}),1.0]])]});}
            extrude(context, id + "F6", {"entities" : qUnion([Q0, Q1, Q2, Q3, Q4, Q5, Q6, Q7, Q8, Q9, Q10, Q11, Q12, Q13, Q14, Q15, Q16, Q17]), "operationType" : NewBodyOperationType.ADD, "depth" : 25.4 * mm, "offsetDistance" : 25.4 * mm});
        }
        {
            var Q0;
            Q0=qCreatedBy(makeId("Front.planeOp"),FACE);
            var Q1;
            Q1=sQuery(id+"F0.wireOp",EDGE,"E23");
            cPlane(context, id + "F7", {"entities" : qUnion([Q0, Q1]), "cplaneType" : CPlaneType.LINE_ANGLE, "offset" : 25.4 * mm, "angle" : 0 * degree, "width" : 152.4 * mm, "height" : 152.4 * mm});
        }
        {
            var Q0;
            Q0=qCreatedBy(id+"F7.planeOp",FACE);
            var sketch = newSketch(context, id + "F8", { "sketchPlane" : qUnion([Q0])});
            skLineSegment(sketch, "E24", {"start": v(0.66, 0) * mm, "end": v(-361.3, 0) * mm});
            skLineSegment(sketch, "E25", {"start": v(-361.3, 0) * mm, "end": v(-263.47, -139.7) * mm});
            skLineSegment(sketch, "E26", {"start": v(-263.47, -139.7) * mm, "end": v(0.66, -139.7) * mm});
            skLineSegment(sketch, "E27", {"start": v(0.66, -139.7) * mm, "end": v(0.66, 0) * mm});
            skLineSegment(sketch, "E28", {"start": v(-285.1, 0) * mm, "end": v(-114.55, 0) * mm});
            skLineSegment(sketch, "E29", {"start": v(-114.55, 0) * mm, "end": v(-630.32, -736.6) * mm});
            skLineSegment(sketch, "E30", {"start": v(-630.32, -736.6) * mm, "end": v(-800.87, -736.6) * mm});
            skLineSegment(sketch, "E31", {"start": v(-800.87, -736.6) * mm, "end": v(-285.1, 0) * mm});
            skLineSegment(sketch, "E32", {"start": v(0.66, -279.4) * mm, "end": v(-812.14, -279.4) * mm});
            skLineSegment(sketch, "E33", {"start": v(-812.14, -279.4) * mm, "end": v(-714.32, -419.1) * mm});
            skLineSegment(sketch, "E34", {"start": v(-714.32, -419.1) * mm, "end": v(0.66, -419.1) * mm});
            skLineSegment(sketch, "E35", {"start": v(0.66, -279.4) * mm, "end": v(0.66, -419.1) * mm});
            skPoint(sketch, "E36", {"position": v(-480.73, -279.4) * mm});
            skLineSegment(sketch, "E37.MirrorCS", {"start": v(0.66, 0) * mm, "end": v(362.6, 0) * mm});
            skLineSegment(sketch, "E38.MirrorCS", {"start": v(362.6, 0) * mm, "end": v(264.79, -139.7) * mm});
            skLineSegment(sketch, "E39.MirrorCS", {"start": v(264.79, -139.7) * mm, "end": v(0.66, -139.7) * mm});
            skLineSegment(sketch, "E40.MirrorCS", {"start": v(115.86, 0) * mm, "end": v(631.64, -736.6) * mm});
            skLineSegment(sketch, "E41.MirrorCS", {"start": v(802.18, -736.6) * mm, "end": v(286.4, 0) * mm});
            skLineSegment(sketch, "E42.MirrorCS", {"start": v(0.66, -279.4) * mm, "end": v(813.46, -279.4) * mm});
            skLineSegment(sketch, "E43.MirrorCS", {"start": v(715.64, -419.1) * mm, "end": v(0.66, -419.1) * mm});
            skLineSegment(sketch, "E44.MirrorCS", {"start": v(813.46, -279.4) * mm, "end": v(715.64, -419.1) * mm});
            skLineSegment(sketch, "E45.MirrorCS", {"start": v(631.64, -736.6) * mm, "end": v(802.18, -736.6) * mm});
            skPoint(sketch, "E46", {"position": v(482.04, -279.4) * mm});
            skSolve(sketch);
        }
        {
            var Q0;
            {var subQ0=sQuery(id+"F8.wireOp",EDGE,"E28");Q0=makeQuery(id+"F8.imprint","IMPRINT",FACE,{"disambiguationData":[TD([[makeQuery(id+"F8.imprint","IMPRINT",EDGE,{"derivedFrom":subQ0}),-1.0]])]});}
            var Q1;
            {var subQ1=sQuery(id+"F8.wireOp",EDGE,"E25");var subQ5=sQuery(id+"F8.wireOp",EDGE,"E26");var subQ6=makeQuery(id+"F8.imprint","INTERSECT",VERTEX,{"derivedFrom":[subQ1,subQ5]});Q1=makeQuery(id+"F8.imprint","IMPRINT",FACE,{"disambiguationData":[TD([[makeQuery(id+"F8.imprint","IMPRINT",EDGE,{"disambiguationData":[TD([[subQ6,1.0]])],"derivedFrom":subQ1}),-1.0]])]});}
            var Q2;
            {var subQ0=sQuery(id+"F8.wireOp",EDGE,"E34");var subQ1=sQuery(id+"F8.wireOp",EDGE,"E29");var subQ2=makeQuery(id+"F8.imprint","INTERSECT",VERTEX,{"derivedFrom":[subQ1,subQ0]});Q2=makeQuery(id+"F8.imprint","IMPRINT",FACE,{"disambiguationData":[TD([[makeQuery(id+"F8.imprint","IMPRINT",EDGE,{"disambiguationData":[TD([[subQ2,1.0]])],"derivedFrom":subQ1}),-1.0]])]});}
            var Q3;
            {var subQ0=sQuery(id+"F8.wireOp",EDGE,"E30");Q3=makeQuery(id+"F8.imprint","IMPRINT",FACE,{"disambiguationData":[TD([[makeQuery(id+"F8.imprint","IMPRINT",EDGE,{"derivedFrom":subQ0}),-1.0]])]});}
            var Q4;
            {var subQ0=sQuery(id+"F8.wireOp",EDGE,"E45.MirrorCS");Q4=makeQuery(id+"F8.imprint","IMPRINT",FACE,{"disambiguationData":[TD([[makeQuery(id+"F8.imprint","IMPRINT",EDGE,{"derivedFrom":subQ0}),1.0]])]});}
            var Q5;
            {var subQ0=sQuery(id+"F8.wireOp",EDGE,"E43.MirrorCS");var subQ1=sQuery(id+"F8.wireOp",EDGE,"E40.MirrorCS");var subQ2=makeQuery(id+"F8.imprint","INTERSECT",VERTEX,{"derivedFrom":[subQ1,subQ0]});Q5=makeQuery(id+"F8.imprint","IMPRINT",FACE,{"disambiguationData":[TD([[makeQuery(id+"F8.imprint","IMPRINT",EDGE,{"disambiguationData":[TD([[subQ2,1.0]])],"derivedFrom":subQ1}),1.0]])]});}
            var Q6;
            {var subQ1=sQuery(id+"F8.wireOp",EDGE,"E38.MirrorCS");var subQ6=sQuery(id+"F8.wireOp",EDGE,"E39.MirrorCS");var subQ9=makeQuery(id+"F8.imprint","INTERSECT",VERTEX,{"derivedFrom":[subQ1,subQ6]});Q6=makeQuery(id+"F8.imprint","IMPRINT",FACE,{"disambiguationData":[TD([[makeQuery(id+"F8.imprint","IMPRINT",EDGE,{"disambiguationData":[TD([[subQ9,1.0]])],"derivedFrom":subQ1}),1.0]])]});}
            var Q7;
            {var subQ0=sQuery(id+"F8.wireOp",EDGE,"E40.MirrorCS");var subQ1=sQuery(id+"F8.wireOp",EDGE,"E37.MirrorCS");var subQ2=makeQuery(id+"F8.imprint","INTERSECT",VERTEX,{"derivedFrom":[subQ1,subQ0]});Q7=makeQuery(id+"F8.imprint","IMPRINT",FACE,{"disambiguationData":[TD([[makeQuery(id+"F8.imprint","IMPRINT",EDGE,{"disambiguationData":[TD([[subQ2,-1.0]])],"derivedFrom":subQ1}),-1.0]])]});}
            extrude(context, id + "F9", {"entities" : qUnion([Q0, Q1, Q2, Q3, Q4, Q5, Q6, Q7]), "depth" : 76.2 * mm, "hasOffset" : true, "offsetDistance" : 76.2 * mm, "offsetOppositeDirection" : true, "hasSecondDirection" : true, "secondDirectionOppositeDirection" : false, "secondDirectionDepth" : 38.1 * mm});
        }
        {
            var Q0;
            {var subQ0=sQuery(id+"F8.wireOp",EDGE,"E28");Q0=makeQuery(id+"F8.imprint","IMPRINT",FACE,{"disambiguationData":[TD([[makeQuery(id+"F8.imprint","IMPRINT",EDGE,{"derivedFrom":subQ0}),-1.0]])]});}
            var Q1;
            {var subQ0=sQuery(id+"F8.wireOp",EDGE,"E27");Q1=makeQuery(id+"F8.imprint","IMPRINT",FACE,{"disambiguationData":[TD([[makeQuery(id+"F8.imprint","IMPRINT",EDGE,{"derivedFrom":subQ0}),1.0]])]});}
            var Q2;
            {var subQ0=sQuery(id+"F8.wireOp",EDGE,"E27");Q2=makeQuery(id+"F8.imprint","IMPRINT",FACE,{"disambiguationData":[TD([[makeQuery(id+"F8.imprint","IMPRINT",EDGE,{"derivedFrom":subQ0}),-1.0]])]});}
            var Q3;
            {var subQ0=sQuery(id+"F8.wireOp",EDGE,"E40.MirrorCS");var subQ1=sQuery(id+"F8.wireOp",EDGE,"E37.MirrorCS");var subQ2=makeQuery(id+"F8.imprint","INTERSECT",VERTEX,{"derivedFrom":[subQ1,subQ0]});Q3=makeQuery(id+"F8.imprint","IMPRINT",FACE,{"disambiguationData":[TD([[makeQuery(id+"F8.imprint","IMPRINT",EDGE,{"disambiguationData":[TD([[subQ2,-1.0]])],"derivedFrom":subQ1}),-1.0]])]});}
            var Q4;
            {var subQ0=sQuery(id+"F8.wireOp",EDGE,"E25");var subQ1=sQuery(id+"F8.wireOp",EDGE,"E24");var subQ2=makeQuery(id+"F8.imprint","INTERSECT",VERTEX,{"derivedFrom":[subQ1,subQ0]});Q4=makeQuery(id+"F8.imprint","IMPRINT",FACE,{"disambiguationData":[TD([[makeQuery(id+"F8.imprint","IMPRINT",EDGE,{"disambiguationData":[TD([[subQ2,-1.0]])],"derivedFrom":subQ0}),1.0]])]});}
            var Q5;
            {var subQ0=sQuery(id+"F8.wireOp",EDGE,"E38.MirrorCS");var subQ1=sQuery(id+"F8.wireOp",EDGE,"E37.MirrorCS");var subQ2=makeQuery(id+"F8.imprint","INTERSECT",VERTEX,{"derivedFrom":[subQ1,subQ0]});Q5=makeQuery(id+"F8.imprint","IMPRINT",FACE,{"disambiguationData":[TD([[makeQuery(id+"F8.imprint","IMPRINT",EDGE,{"disambiguationData":[TD([[subQ2,1.0]])],"derivedFrom":subQ1}),-1.0]])]});}
            var Q6;
            {var subQ5=sQuery(id+"F8.wireOp",EDGE,"E35");Q6=makeQuery(id+"F8.imprint","IMPRINT",FACE,{"disambiguationData":[TD([[makeQuery(id+"F8.imprint","IMPRINT",EDGE,{"derivedFrom":subQ5}),-1.0]])]});}
            var Q7;
            {var subQ0=sQuery(id+"F8.wireOp",EDGE,"E35");Q7=makeQuery(id+"F8.imprint","IMPRINT",FACE,{"disambiguationData":[TD([[makeQuery(id+"F8.imprint","IMPRINT",EDGE,{"derivedFrom":subQ0}),1.0]])]});}
            var Q8;
            {var subQ0=sQuery(id+"F8.wireOp",EDGE,"E43.MirrorCS");var subQ1=sQuery(id+"F8.wireOp",EDGE,"E40.MirrorCS");var subQ2=makeQuery(id+"F8.imprint","INTERSECT",VERTEX,{"derivedFrom":[subQ1,subQ0]});Q8=makeQuery(id+"F8.imprint","IMPRINT",FACE,{"disambiguationData":[TD([[makeQuery(id+"F8.imprint","IMPRINT",EDGE,{"disambiguationData":[TD([[subQ2,1.0]])],"derivedFrom":subQ1}),1.0]])]});}
            var Q9;
            {var subQ5=sQuery(id+"F8.wireOp",EDGE,"E44.MirrorCS");Q9=makeQuery(id+"F8.imprint","IMPRINT",FACE,{"disambiguationData":[TD([[makeQuery(id+"F8.imprint","IMPRINT",EDGE,{"derivedFrom":subQ5}),-1.0]])]});}
            var Q10;
            {var subQ0=sQuery(id+"F8.wireOp",EDGE,"E34");var subQ1=sQuery(id+"F8.wireOp",EDGE,"E29");var subQ2=makeQuery(id+"F8.imprint","INTERSECT",VERTEX,{"derivedFrom":[subQ1,subQ0]});Q10=makeQuery(id+"F8.imprint","IMPRINT",FACE,{"disambiguationData":[TD([[makeQuery(id+"F8.imprint","IMPRINT",EDGE,{"disambiguationData":[TD([[subQ2,1.0]])],"derivedFrom":subQ1}),-1.0]])]});}
            var Q11;
            {var subQ5=sQuery(id+"F8.wireOp",EDGE,"E33");Q11=makeQuery(id+"F8.imprint","IMPRINT",FACE,{"disambiguationData":[TD([[makeQuery(id+"F8.imprint","IMPRINT",EDGE,{"derivedFrom":subQ5}),1.0]])]});}
            extrude(context, id + "F10", {"entities" : qUnion([Q0, Q1, Q2, Q3, Q4, Q5, Q6, Q7, Q8, Q9, Q10, Q11]), "depth" : 38.1 * mm, "offsetDistance" : 25.4 * mm});
        }
        {
            var Q0;
            Q0=qCreatedBy(makeId("Right.planeOp"),FACE);
            var sketch = newSketch(context, id + "F11", { "sketchPlane" : qUnion([Q0])});
            skLineSegment(sketch, "E47", {"start": v(571.5, 0) * mm, "end": v(406.22, -279.4) * mm});
            skLineSegment(sketch, "E48", {"start": v(406.22, -279.4) * mm, "end": v(361.95, -279.4) * mm});
            skLineSegment(sketch, "E49", {"start": v(361.95, -279.4) * mm, "end": v(527.23, 0) * mm});
            skLineSegment(sketch, "E50", {"start": v(527.23, 0) * mm, "end": v(571.5, 0) * mm});
            skLineSegment(sketch, "E51", {"start": v(571.5, 0) * mm, "end": v(546.71, 0) * mm});
            skSolve(sketch);
        }
        {
            var Q0;
            Q0 = qSketchRegion(id + "F11", true);
            extrude(context, id + "F12", {"entities" : qUnion([Q0]), "depth" : 139.7 * mm, "offsetDistance" : 25.4 * mm, "symmetric" : true});
        }
    });
